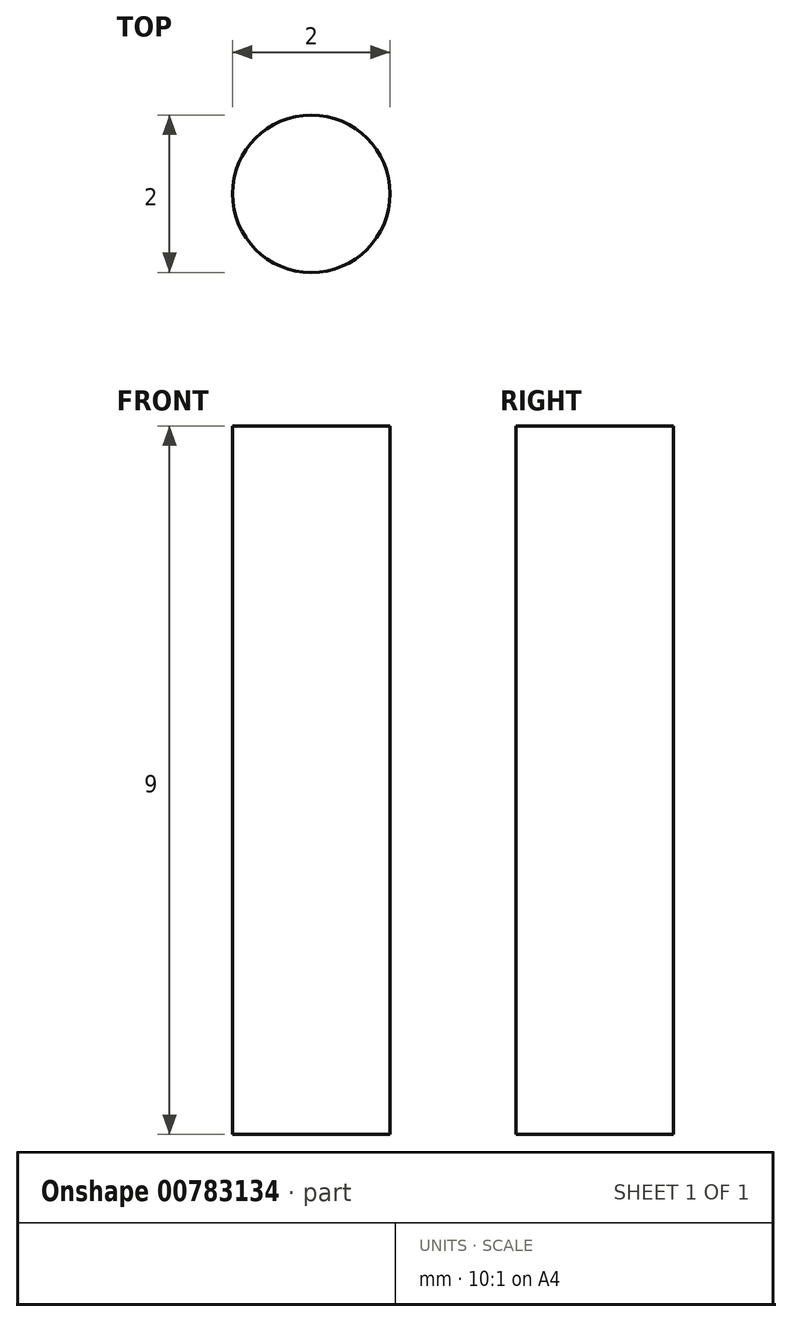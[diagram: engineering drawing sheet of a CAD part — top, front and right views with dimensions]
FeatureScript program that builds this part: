
annotation { "Feature Type Name" : "Feature", "Feature Type Description" : "" }
export const myFeature = defineFeature(function(context is Context, id is Id, definition is map)
    precondition{}
    {
        {
            var Q0;
            Q0=qCreatedBy(makeId("Top.planeOp"),FACE);
            var sketch = newSketch(context, id + "F0", { "sketchPlane" : qUnion([Q0])});
            skCircle(sketch, "E0", {"center": v(0, 0) * mm, "radius": 1 * mm});
            skSolve(sketch);
        }
        {
            var Q0;
            Q0=makeQuery(id+"F0.imprint","IMPRINT",FACE,{"disambiguationData":[TD([[makeQuery(id+"F0.imprint","IMPRINT",EDGE,{"derivedFrom":sQuery(id+"F0.wireOp",EDGE,"E0")}),1.0]])]});
            extrude(context, id + "F1", {"entities" : qUnion([Q0]), "depth" : 9 * mm, "offsetDistance" : 25 * mm});
        }
    });
